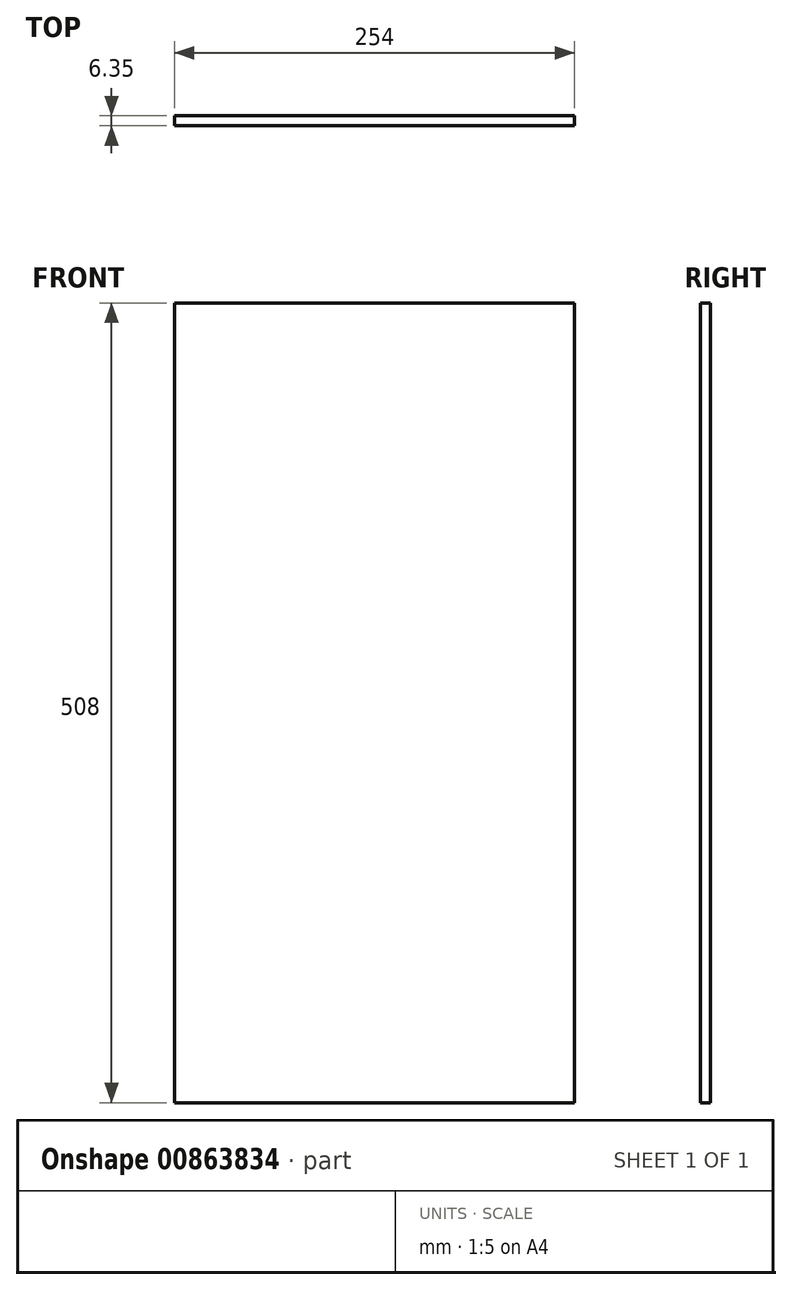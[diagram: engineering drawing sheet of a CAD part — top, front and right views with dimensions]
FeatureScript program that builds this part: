
annotation { "Feature Type Name" : "Feature", "Feature Type Description" : "" }
export const myFeature = defineFeature(function(context is Context, id is Id, definition is map)
    precondition{}
    {
        {
            var Q0;
            Q0=qCreatedBy(makeId("Front.planeOp"),FACE);
            var sketch = newSketch(context, id + "F0", { "sketchPlane" : qUnion([Q0])});
            skLineSegment(sketch, "E0.bottom", {"start": v(0, 0) * mm, "end": v(-254, 0) * mm});
            skLineSegment(sketch, "E0.top", {"start": v(0, 508) * mm, "end": v(-254, 508) * mm});
            skLineSegment(sketch, "E0.left", {"start": v(0, 0) * mm, "end": v(0, 508) * mm});
            skLineSegment(sketch, "E0.right", {"start": v(-254, 0) * mm, "end": v(-254, 508) * mm});
            skSolve(sketch);
        }
        {
            var Q0;
            Q0=qSketchRegion(id+"F0",true);
            extrude(context, id + "F1", {"entities" : qUnion([Q0]), "oppositeDirection" : true, "depth" : 6.35 * mm, "offsetDistance" : 25.4 * mm});
        }
    });
